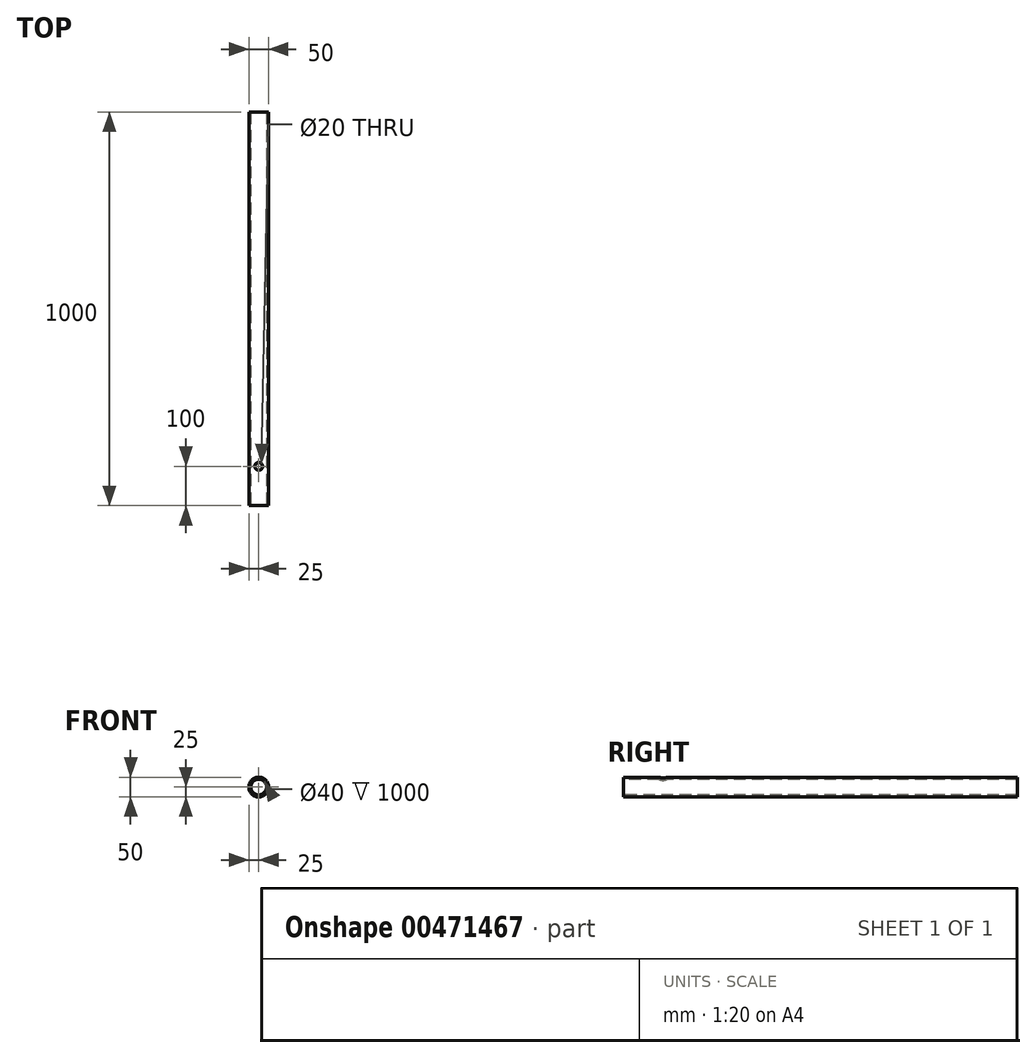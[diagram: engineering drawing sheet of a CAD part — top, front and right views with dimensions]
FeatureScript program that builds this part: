
annotation { "Feature Type Name" : "Feature", "Feature Type Description" : "" }
export const myFeature = defineFeature(function(context is Context, id is Id, definition is map)
    precondition{}
    {
        {
            var Q0;
            Q0=qCreatedBy(makeId("Front.planeOp"),FACE);
            var sketch = newSketch(context, id + "F0", { "sketchPlane" : qUnion([Q0])});
            skCircle(sketch, "E0", {"center": v(0, 0) * mm, "radius": 25 * mm});
            skSolve(sketch);
        }
        {
            var Q0;
            Q0=makeQuery(id+"F0.imprint","IMPRINT",FACE,{"disambiguationData":[TD([[makeQuery(id+"F0.imprint","IMPRINT",EDGE,{"derivedFrom":sQuery(id+"F0.wireOp",EDGE,"E0")}),1.0]])]});
            var Q1;
            Q1=sQuery(id+"F0.wireOp",EDGE,"E0");
            extrude(context, id + "F1", {"entities" : qUnion([Q0]), "surfaceEntities" : qUnion([Q1]), "oppositeDirection" : true, "depth" : 1000 * mm});
        }
        {
            var Q0;
            Q0=qCreatedBy(makeId("Front.planeOp"),FACE);
            var sketch = newSketch(context, id + "F2", { "sketchPlane" : qUnion([Q0])});
            skCircle(sketch, "E1", {"center": v(0, 0) * mm, "radius": 20 * mm});
            skSolve(sketch);
        }
        {
            var Q0;
            Q0=makeQuery(id+"F2.imprint","IMPRINT",FACE,{"disambiguationData":[TD([[makeQuery(id+"F2.imprint","IMPRINT",EDGE,{"derivedFrom":sQuery(id+"F2.wireOp",EDGE,"E1")}),1.0]])]});
            var Q1;
            Q1=sQuery(id+"F2.wireOp",EDGE,"E1");
            extrude(context, id + "F3", {"entities" : qUnion([Q0]), "operationType" : NewBodyOperationType.REMOVE, "surfaceEntities" : qUnion([Q1]), "endBound" : BoundingType.THROUGH_ALL, "oppositeDirection" : true, "depth" : 1200 * mm});
        }
        {
            var Q0;
            Q0=qCreatedBy(makeId("Top.planeOp"),FACE);
            var sketch = newSketch(context, id + "F4", { "sketchPlane" : qUnion([Q0])});
            skCircle(sketch, "E2", {"center": v(0, 100) * mm, "radius": 10 * mm});
            skSolve(sketch);
        }
        {
            var Q0;
            Q0 = qSketchRegion(id + "F4", true);
            extrude(context, id + "F5", {"entities" : qUnion([Q0]), "operationType" : NewBodyOperationType.REMOVE, "depth" : 25.4 * mm});
        }
    });
